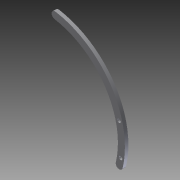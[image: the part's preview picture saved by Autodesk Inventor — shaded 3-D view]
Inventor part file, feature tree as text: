
AUTODESK INVENTOR PART (.ipt)
format: ipt  version: 2012 (Build 160160000, 160)  size: 90,112 bytes
history: native  units: in
note: dims shown in document units (in); Inventor stores cm internally (conversion verified against a paired STEP export)
features: extrude x1, sketch x1
ambient origin geometry x8: Origin, YZ Plane, XZ Plane, XY Plane, X Axis, Y Axis, Z Axis, Center Point
bodies: Solid1 (feature_tree)
feature tree (2):
  extrude  "Extrusion1"  Depth=12.0in
  sketch  "Sketch1"  dims[d0=11.0in d1=12.0in d2=0.5in d3=7.0in d4=1.0in d5=0.25in d6=0.25in d7=0.125in d8=0.5in d10=0.125in d12=2.25in d13=0.25in d14=0.0in]
